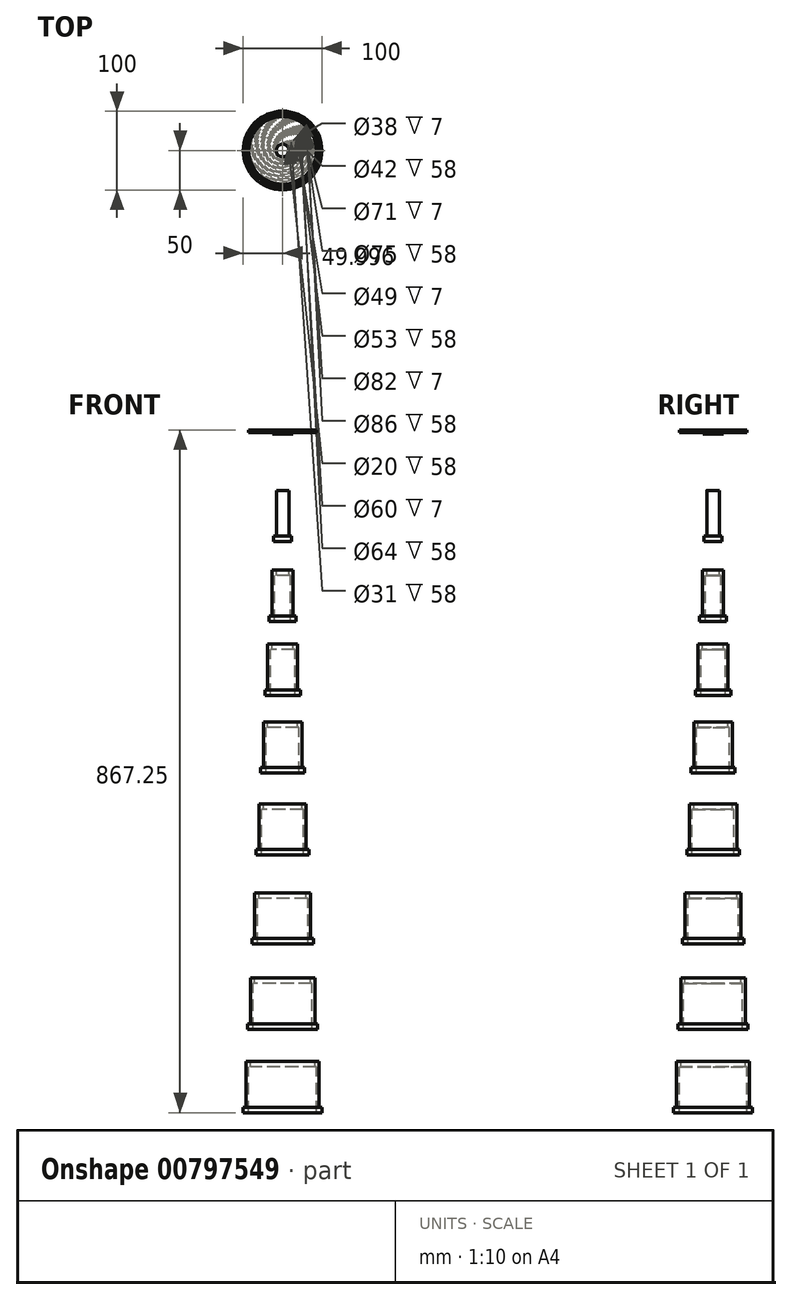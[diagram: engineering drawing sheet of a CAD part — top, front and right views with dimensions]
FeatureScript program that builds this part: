
annotation { "Feature Type Name" : "Feature", "Feature Type Description" : "" }
export const myFeature = defineFeature(function(context is Context, id is Id, definition is map)
    precondition{}
    {
        {
            var Q0;
            Q0=qCreatedBy(makeId("Front.planeOp"),FACE);
            var sketch = newSketch(context, id + "F0", { "sketchPlane" : qUnion([Q0])});
            skLineSegment(sketch, "E0", {"start": v(420.63, 136.3) * mm, "end": v(420.63, -631.8) * mm});
            skLineSegment(sketch, "E1", {"start": v(420.63, 28.97) * mm, "end": v(412.63, 28.97) * mm});
            skLineSegment(sketch, "E2", {"start": v(412.63, -34.03) * mm, "end": v(411.13, -34.03) * mm});
            skLineSegment(sketch, "E3", {"start": v(411.13, -34.03) * mm, "end": v(411.13, -41.03) * mm});
            skLineSegment(sketch, "E4", {"start": v(411.13, -41.03) * mm, "end": v(420.63, -41.03) * mm});
            skLineSegment(sketch, "E5", {"start": v(411.13, -54.93) * mm, "end": v(411.13, -61.93) * mm});
            skLineSegment(sketch, "E6", {"start": v(411.13, -61.93) * mm, "end": v(409.63, -61.93) * mm});
            skLineSegment(sketch, "E7", {"start": v(407.63, -112.93) * mm, "end": v(406.13, -112.93) * mm});
            skLineSegment(sketch, "E8", {"start": v(406.13, -112.93) * mm, "end": v(406.13, -119.93) * mm});
            skLineSegment(sketch, "E9", {"start": v(412.63, 52.64) * mm, "end": v(412.63, 57.64) * mm});
            skLineSegment(sketch, "E10", {"start": v(412.63, 57.64) * mm, "end": v(377.63, 57.64) * mm});
            skLineSegment(sketch, "E11", {"start": v(377.63, 57.64) * mm, "end": v(377.63, 54.64) * mm});
            skLineSegment(sketch, "E12", {"start": v(412.63, 52.64) * mm, "end": v(407.63, 52.64) * mm});
            skLineSegment(sketch, "E13", {"start": v(377.63, 54.64) * mm, "end": v(407.63, 54.64) * mm});
            skLineSegment(sketch, "E14", {"start": v(412.63, -34.03) * mm, "end": v(412.63, 28.97) * mm});
            skLineSegment(sketch, "E15", {"start": v(407.63, -112.93) * mm, "end": v(407.63, -54.93) * mm});
            skLineSegment(sketch, "E16", {"start": v(409.63, -119.93) * mm, "end": v(409.63, -61.93) * mm});
            skLineSegment(sketch, "E17", {"start": v(411.13, -34.03) * mm, "end": v(409.63, -34.03) * mm});
            skLineSegment(sketch, "E18", {"start": v(409.63, -34.03) * mm, "end": v(409.63, -41.03) * mm});
            skLineSegment(sketch, "E19", {"start": v(409.63, -41.03) * mm, "end": v(411.13, -41.03) * mm});
            skLineSegment(sketch, "E20", {"start": v(412.63, -61.93) * mm, "end": v(411.13, -61.93) * mm});
            skLineSegment(sketch, "E21", {"start": v(412.63, -61.93) * mm, "end": v(412.63, -54.93) * mm});
            skLineSegment(sketch, "E22", {"start": v(412.63, -54.93) * mm, "end": v(411.13, -54.93) * mm});
            skLineSegment(sketch, "E23", {"start": v(406.13, -119.93) * mm, "end": v(404.63, -119.93) * mm});
            skLineSegment(sketch, "E24", {"start": v(404.63, -119.93) * mm, "end": v(404.63, -112.93) * mm});
            skLineSegment(sketch, "E25", {"start": v(404.63, -112.93) * mm, "end": v(406.13, -112.93) * mm});
            skLineSegment(sketch, "E26", {"start": v(409.63, -61.93) * mm, "end": v(409.63, -54.93) * mm});
            skLineSegment(sketch, "E27", {"start": v(407.63, -112.93) * mm, "end": v(407.63, -119.93) * mm});
            skLineSegment(sketch, "E28", {"start": v(406.13, -119.93) * mm, "end": v(407.63, -119.93) * mm});
            skLineSegment(sketch, "E29", {"start": v(407.63, -119.93) * mm, "end": v(409.63, -119.93) * mm});
            skLineSegment(sketch, "E30", {"start": v(411.13, -54.93) * mm, "end": v(409.63, -54.93) * mm});
            skLineSegment(sketch, "E31", {"start": v(409.63, -54.93) * mm, "end": v(407.63, -54.93) * mm});
            skLineSegment(sketch, "E32", {"start": v(381.13, -577.9) * mm, "end": v(381.13, -584.9) * mm});
            skLineSegment(sketch, "E33", {"start": v(381.13, -584.9) * mm, "end": v(379.63, -584.9) * mm});
            skLineSegment(sketch, "E34", {"start": v(377.63, -632.9) * mm, "end": v(377.63, -577.9) * mm});
            skLineSegment(sketch, "E35", {"start": v(379.63, -642.9) * mm, "end": v(379.63, -584.9) * mm});
            skLineSegment(sketch, "E36", {"start": v(382.63, -584.9) * mm, "end": v(381.13, -584.9) * mm});
            skLineSegment(sketch, "E37", {"start": v(382.63, -584.9) * mm, "end": v(382.63, -577.9) * mm});
            skLineSegment(sketch, "E38", {"start": v(382.63, -577.9) * mm, "end": v(381.13, -577.9) * mm});
            skLineSegment(sketch, "E39", {"start": v(379.63, -584.9) * mm, "end": v(379.63, -577.9) * mm});
            skLineSegment(sketch, "E40", {"start": v(381.13, -577.9) * mm, "end": v(379.63, -577.9) * mm});
            skLineSegment(sketch, "E41", {"start": v(379.63, -577.9) * mm, "end": v(377.63, -577.9) * mm});
            skLineSegment(sketch, "E42.bottom", {"start": v(378.63, -642.9) * mm, "end": v(420.63, -642.9) * mm});
            skLineSegment(sketch, "E42.top", {"start": v(378.63, -649.9) * mm, "end": v(420.63, -649.9) * mm});
            skLineSegment(sketch, "E42.left", {"start": v(378.63, -642.9) * mm, "end": v(378.63, -649.9) * mm});
            skLineSegment(sketch, "E42.right", {"start": v(420.63, -642.9) * mm, "end": v(420.63, -649.9) * mm});
            skLineSegment(sketch, "E43", {"start": v(379.63, -642.9) * mm, "end": v(378.63, -642.9) * mm});
            skLineSegment(sketch, "E44", {"start": v(378.63, -649.9) * mm, "end": v(374.63, -649.9) * mm});
            skLineSegment(sketch, "E45", {"start": v(374.63, -649.9) * mm, "end": v(374.63, -632.9) * mm});
            skLineSegment(sketch, "E46", {"start": v(374.63, -632.9) * mm, "end": v(377.63, -632.9) * mm});
            skLineSegment(sketch, "E47", {"start": v(407.63, 54.64) * mm, "end": v(407.63, 52.64) * mm});
            skLineSegment(sketch, "E48.top", {"start": v(412.63, -64.93) * mm, "end": v(411.13, -64.93) * mm});
            skLineSegment(sketch, "E48.left", {"start": v(412.63, -61.93) * mm, "end": v(412.63, -64.93) * mm});
            skLineSegment(sketch, "E48.right", {"start": v(411.13, -61.93) * mm, "end": v(411.13, -64.93) * mm});
            skLineSegment(sketch, "E49", {"start": v(406.13, -136.28) * mm, "end": v(406.13, -143.28) * mm});
            skLineSegment(sketch, "E50", {"start": v(406.13, -143.28) * mm, "end": v(404.63, -143.28) * mm});
            skLineSegment(sketch, "E51", {"start": v(402.63, -194.28) * mm, "end": v(401.13, -194.28) * mm});
            skLineSegment(sketch, "E52", {"start": v(401.13, -194.28) * mm, "end": v(401.13, -201.28) * mm});
            skLineSegment(sketch, "E53", {"start": v(402.63, -194.28) * mm, "end": v(402.63, -136.28) * mm});
            skLineSegment(sketch, "E54", {"start": v(404.63, -201.28) * mm, "end": v(404.63, -143.28) * mm});
            skLineSegment(sketch, "E55", {"start": v(407.63, -143.28) * mm, "end": v(406.13, -143.28) * mm});
            skLineSegment(sketch, "E56", {"start": v(407.63, -143.28) * mm, "end": v(407.63, -136.28) * mm});
            skLineSegment(sketch, "E57", {"start": v(407.63, -136.28) * mm, "end": v(406.13, -136.28) * mm});
            skLineSegment(sketch, "E58", {"start": v(401.13, -201.28) * mm, "end": v(399.63, -201.28) * mm});
            skLineSegment(sketch, "E59", {"start": v(399.63, -201.28) * mm, "end": v(399.63, -194.28) * mm});
            skLineSegment(sketch, "E60", {"start": v(399.63, -194.28) * mm, "end": v(401.13, -194.28) * mm});
            skLineSegment(sketch, "E61", {"start": v(404.63, -143.28) * mm, "end": v(404.63, -136.28) * mm});
            skLineSegment(sketch, "E62", {"start": v(402.63, -194.28) * mm, "end": v(402.63, -201.28) * mm});
            skLineSegment(sketch, "E63", {"start": v(401.13, -201.28) * mm, "end": v(402.63, -201.28) * mm});
            skLineSegment(sketch, "E64", {"start": v(402.63, -201.28) * mm, "end": v(404.63, -201.28) * mm});
            skLineSegment(sketch, "E65", {"start": v(406.13, -136.28) * mm, "end": v(404.63, -136.28) * mm});
            skLineSegment(sketch, "E66", {"start": v(404.63, -136.28) * mm, "end": v(402.63, -136.28) * mm});
            skLineSegment(sketch, "E67.top", {"start": v(407.63, -146.28) * mm, "end": v(406.13, -146.28) * mm});
            skLineSegment(sketch, "E67.left", {"start": v(407.63, -143.28) * mm, "end": v(407.63, -146.28) * mm});
            skLineSegment(sketch, "E67.right", {"start": v(406.13, -143.28) * mm, "end": v(406.13, -146.28) * mm});
            skLineSegment(sketch, "E68", {"start": v(401.13, -219.28) * mm, "end": v(401.13, -226.28) * mm});
            skLineSegment(sketch, "E69", {"start": v(401.13, -226.28) * mm, "end": v(399.63, -226.28) * mm});
            skLineSegment(sketch, "E70", {"start": v(397.63, -277.28) * mm, "end": v(396.13, -277.28) * mm});
            skLineSegment(sketch, "E71", {"start": v(396.13, -277.28) * mm, "end": v(396.13, -284.28) * mm});
            skLineSegment(sketch, "E72", {"start": v(397.63, -277.28) * mm, "end": v(397.63, -219.28) * mm});
            skLineSegment(sketch, "E73", {"start": v(399.63, -284.28) * mm, "end": v(399.63, -226.28) * mm});
            skLineSegment(sketch, "E74", {"start": v(402.63, -226.28) * mm, "end": v(401.13, -226.28) * mm});
            skLineSegment(sketch, "E75", {"start": v(402.63, -226.28) * mm, "end": v(402.63, -219.28) * mm});
            skLineSegment(sketch, "E76", {"start": v(402.63, -219.28) * mm, "end": v(401.13, -219.28) * mm});
            skLineSegment(sketch, "E77", {"start": v(396.13, -284.28) * mm, "end": v(394.63, -284.28) * mm});
            skLineSegment(sketch, "E78", {"start": v(394.63, -284.28) * mm, "end": v(394.63, -277.28) * mm});
            skLineSegment(sketch, "E79", {"start": v(394.63, -277.28) * mm, "end": v(396.13, -277.28) * mm});
            skLineSegment(sketch, "E80", {"start": v(399.63, -226.28) * mm, "end": v(399.63, -219.28) * mm});
            skLineSegment(sketch, "E81", {"start": v(397.63, -277.28) * mm, "end": v(397.63, -284.28) * mm});
            skLineSegment(sketch, "E82", {"start": v(396.13, -284.28) * mm, "end": v(397.63, -284.28) * mm});
            skLineSegment(sketch, "E83", {"start": v(397.63, -284.28) * mm, "end": v(399.63, -284.28) * mm});
            skLineSegment(sketch, "E84", {"start": v(401.13, -219.28) * mm, "end": v(399.63, -219.28) * mm});
            skLineSegment(sketch, "E85", {"start": v(399.63, -219.28) * mm, "end": v(397.63, -219.28) * mm});
            skLineSegment(sketch, "E86.top", {"start": v(402.63, -229.28) * mm, "end": v(401.13, -229.28) * mm});
            skLineSegment(sketch, "E86.left", {"start": v(402.63, -226.28) * mm, "end": v(402.63, -229.28) * mm});
            skLineSegment(sketch, "E86.right", {"start": v(401.13, -226.28) * mm, "end": v(401.13, -229.28) * mm});
            skLineSegment(sketch, "E87", {"start": v(396.13, -311.87) * mm, "end": v(396.13, -318.87) * mm});
            skLineSegment(sketch, "E88", {"start": v(396.13, -318.87) * mm, "end": v(394.63, -318.87) * mm});
            skLineSegment(sketch, "E89", {"start": v(392.63, -369.87) * mm, "end": v(391.13, -369.87) * mm});
            skLineSegment(sketch, "E90", {"start": v(391.13, -369.87) * mm, "end": v(391.13, -376.87) * mm});
            skLineSegment(sketch, "E91", {"start": v(392.63, -369.87) * mm, "end": v(392.63, -311.87) * mm});
            skLineSegment(sketch, "E92", {"start": v(394.63, -376.87) * mm, "end": v(394.63, -318.87) * mm});
            skLineSegment(sketch, "E93", {"start": v(397.63, -318.87) * mm, "end": v(396.13, -318.87) * mm});
            skLineSegment(sketch, "E94", {"start": v(397.63, -318.87) * mm, "end": v(397.63, -311.87) * mm});
            skLineSegment(sketch, "E95", {"start": v(397.63, -311.87) * mm, "end": v(396.13, -311.87) * mm});
            skLineSegment(sketch, "E96", {"start": v(391.13, -376.87) * mm, "end": v(389.63, -376.87) * mm});
            skLineSegment(sketch, "E97", {"start": v(389.63, -376.87) * mm, "end": v(389.63, -369.87) * mm});
            skLineSegment(sketch, "E98", {"start": v(389.63, -369.87) * mm, "end": v(391.13, -369.87) * mm});
            skLineSegment(sketch, "E99", {"start": v(394.63, -318.87) * mm, "end": v(394.63, -311.87) * mm});
            skLineSegment(sketch, "E100", {"start": v(392.63, -369.87) * mm, "end": v(392.63, -376.87) * mm});
            skLineSegment(sketch, "E101", {"start": v(391.13, -376.87) * mm, "end": v(392.63, -376.87) * mm});
            skLineSegment(sketch, "E102", {"start": v(392.63, -376.87) * mm, "end": v(394.63, -376.87) * mm});
            skLineSegment(sketch, "E103", {"start": v(396.13, -311.87) * mm, "end": v(394.63, -311.87) * mm});
            skLineSegment(sketch, "E104", {"start": v(394.63, -311.87) * mm, "end": v(392.63, -311.87) * mm});
            skLineSegment(sketch, "E105.top", {"start": v(397.63, -321.87) * mm, "end": v(396.13, -321.87) * mm});
            skLineSegment(sketch, "E105.left", {"start": v(397.63, -318.87) * mm, "end": v(397.63, -321.87) * mm});
            skLineSegment(sketch, "E105.right", {"start": v(396.13, -318.87) * mm, "end": v(396.13, -321.87) * mm});
            skLineSegment(sketch, "E106", {"start": v(391.13, -394.77) * mm, "end": v(391.13, -401.77) * mm});
            skLineSegment(sketch, "E107", {"start": v(391.13, -401.77) * mm, "end": v(389.63, -401.77) * mm});
            skLineSegment(sketch, "E108", {"start": v(387.63, -452.77) * mm, "end": v(386.13, -452.77) * mm});
            skLineSegment(sketch, "E109", {"start": v(386.13, -452.77) * mm, "end": v(386.13, -459.77) * mm});
            skLineSegment(sketch, "E110", {"start": v(387.63, -452.77) * mm, "end": v(387.63, -394.77) * mm});
            skLineSegment(sketch, "E111", {"start": v(389.63, -459.77) * mm, "end": v(389.63, -401.77) * mm});
            skLineSegment(sketch, "E112", {"start": v(392.63, -401.77) * mm, "end": v(391.13, -401.77) * mm});
            skLineSegment(sketch, "E113", {"start": v(392.63, -401.77) * mm, "end": v(392.63, -394.77) * mm});
            skLineSegment(sketch, "E114", {"start": v(392.63, -394.77) * mm, "end": v(391.13, -394.77) * mm});
            skLineSegment(sketch, "E115", {"start": v(386.13, -459.77) * mm, "end": v(384.63, -459.77) * mm});
            skLineSegment(sketch, "E116", {"start": v(384.63, -459.77) * mm, "end": v(384.63, -452.77) * mm});
            skLineSegment(sketch, "E117", {"start": v(384.63, -452.77) * mm, "end": v(386.13, -452.77) * mm});
            skLineSegment(sketch, "E118", {"start": v(389.63, -401.77) * mm, "end": v(389.63, -394.77) * mm});
            skLineSegment(sketch, "E119", {"start": v(387.63, -452.77) * mm, "end": v(387.63, -459.77) * mm});
            skLineSegment(sketch, "E120", {"start": v(386.13, -459.77) * mm, "end": v(387.63, -459.77) * mm});
            skLineSegment(sketch, "E121", {"start": v(387.63, -459.77) * mm, "end": v(389.63, -459.77) * mm});
            skLineSegment(sketch, "E122", {"start": v(391.13, -394.77) * mm, "end": v(389.63, -394.77) * mm});
            skLineSegment(sketch, "E123", {"start": v(389.63, -394.77) * mm, "end": v(387.63, -394.77) * mm});
            skLineSegment(sketch, "E124.top", {"start": v(392.63, -404.77) * mm, "end": v(391.13, -404.77) * mm});
            skLineSegment(sketch, "E124.left", {"start": v(392.63, -401.77) * mm, "end": v(392.63, -404.77) * mm});
            skLineSegment(sketch, "E124.right", {"start": v(391.13, -401.77) * mm, "end": v(391.13, -404.77) * mm});
            skLineSegment(sketch, "E125", {"start": v(386.13, -485.67) * mm, "end": v(386.13, -492.67) * mm});
            skLineSegment(sketch, "E126", {"start": v(386.13, -492.67) * mm, "end": v(384.63, -492.67) * mm});
            skLineSegment(sketch, "E127", {"start": v(382.63, -543.67) * mm, "end": v(381.13, -543.67) * mm});
            skLineSegment(sketch, "E128", {"start": v(381.13, -543.67) * mm, "end": v(381.13, -550.67) * mm});
            skLineSegment(sketch, "E129", {"start": v(382.63, -543.67) * mm, "end": v(382.63, -485.67) * mm});
            skLineSegment(sketch, "E130", {"start": v(384.63, -550.67) * mm, "end": v(384.63, -492.67) * mm});
            skLineSegment(sketch, "E131", {"start": v(387.63, -492.67) * mm, "end": v(386.13, -492.67) * mm});
            skLineSegment(sketch, "E132", {"start": v(387.63, -492.67) * mm, "end": v(387.63, -485.67) * mm});
            skLineSegment(sketch, "E133", {"start": v(387.63, -485.67) * mm, "end": v(386.13, -485.67) * mm});
            skLineSegment(sketch, "E134", {"start": v(381.13, -550.67) * mm, "end": v(379.63, -550.67) * mm});
            skLineSegment(sketch, "E135", {"start": v(379.63, -550.67) * mm, "end": v(379.63, -543.67) * mm});
            skLineSegment(sketch, "E136", {"start": v(379.63, -543.67) * mm, "end": v(381.13, -543.67) * mm});
            skLineSegment(sketch, "E137", {"start": v(384.63, -492.67) * mm, "end": v(384.63, -485.67) * mm});
            skLineSegment(sketch, "E138", {"start": v(382.63, -543.67) * mm, "end": v(382.63, -550.67) * mm});
            skLineSegment(sketch, "E139", {"start": v(381.13, -550.67) * mm, "end": v(382.63, -550.67) * mm});
            skLineSegment(sketch, "E140", {"start": v(382.63, -550.67) * mm, "end": v(384.63, -550.67) * mm});
            skLineSegment(sketch, "E141", {"start": v(386.13, -485.67) * mm, "end": v(384.63, -485.67) * mm});
            skLineSegment(sketch, "E142", {"start": v(384.63, -485.67) * mm, "end": v(382.63, -485.67) * mm});
            skLineSegment(sketch, "E143.top", {"start": v(387.63, -495.67) * mm, "end": v(386.13, -495.67) * mm});
            skLineSegment(sketch, "E143.left", {"start": v(387.63, -492.67) * mm, "end": v(387.63, -495.67) * mm});
            skLineSegment(sketch, "E143.right", {"start": v(386.13, -492.67) * mm, "end": v(386.13, -495.67) * mm});
            skLineSegment(sketch, "E144.left", {"start": v(420.63, 28.97) * mm, "end": v(420.63, 18.97) * mm});
            skLineSegment(sketch, "E145", {"start": v(762.6, 130.32) * mm, "end": v(762.6, -637.77) * mm, "construction": true});
            skLineSegment(sketch, "E146", {"start": v(762.6, -10.86) * mm, "end": v(754.6, -10.86) * mm});
            skLineSegment(sketch, "E147", {"start": v(754.6, -10.86) * mm, "end": v(754.6, -68.86) * mm});
            skLineSegment(sketch, "E148", {"start": v(754.6, -68.86) * mm, "end": v(752.6, -68.86) * mm});
            skLineSegment(sketch, "E149", {"start": v(752.6, -68.86) * mm, "end": v(751.1, -68.86) * mm});
            skLineSegment(sketch, "E150", {"start": v(751.1, -68.86) * mm, "end": v(751.1, -75.86) * mm});
            skLineSegment(sketch, "E151", {"start": v(751.1, -75.86) * mm, "end": v(762.6, -75.86) * mm});
            skLineSegment(sketch, "E152", {"start": v(762.6, -75.86) * mm, "end": v(762.6, -10.86) * mm});
            skLineSegment(sketch, "E153", {"start": v(754.6, -112.1) * mm, "end": v(752.6, -112.1) * mm});
            skLineSegment(sketch, "E154", {"start": v(752.6, -112.1) * mm, "end": v(751.1, -112.1) * mm});
            skLineSegment(sketch, "E155", {"start": v(751.1, -112.1) * mm, "end": v(749.1, -112.1) * mm});
            skLineSegment(sketch, "E156", {"start": v(749.1, -112.1) * mm, "end": v(749.1, -170.1) * mm});
            skLineSegment(sketch, "E157", {"start": v(749.1, -170.1) * mm, "end": v(747.1, -170.1) * mm});
            skLineSegment(sketch, "E158", {"start": v(747.1, -170.1) * mm, "end": v(745.6, -170.1) * mm});
            skLineSegment(sketch, "E159", {"start": v(745.6, -170.1) * mm, "end": v(745.6, -177.1) * mm});
            skLineSegment(sketch, "E160", {"start": v(754.6, -112.1) * mm, "end": v(754.6, -119.1) * mm});
            skLineSegment(sketch, "E161", {"start": v(754.6, -119.1) * mm, "end": v(752.6, -119.1) * mm});
            skLineSegment(sketch, "E162", {"start": v(752.6, -119.1) * mm, "end": v(752.6, -177.1) * mm});
            skLineSegment(sketch, "E163", {"start": v(752.6, -177.1) * mm, "end": v(745.6, -177.1) * mm});
            skLineSegment(sketch, "E164", {"start": v(749.1, -206.1) * mm, "end": v(747.1, -206.1) * mm});
            skLineSegment(sketch, "E165", {"start": v(747.1, -206.1) * mm, "end": v(745.6, -206.1) * mm});
            skLineSegment(sketch, "E166", {"start": v(745.6, -206.1) * mm, "end": v(743.6, -206.1) * mm});
            skLineSegment(sketch, "E167", {"start": v(743.6, -206.1) * mm, "end": v(743.6, -264.1) * mm});
            skLineSegment(sketch, "E168", {"start": v(743.6, -264.1) * mm, "end": v(741.6, -264.1) * mm});
            skLineSegment(sketch, "E169", {"start": v(741.6, -264.1) * mm, "end": v(740.1, -264.1) * mm});
            skLineSegment(sketch, "E170", {"start": v(740.1, -264.1) * mm, "end": v(740.1, -271.1) * mm});
            skLineSegment(sketch, "E171", {"start": v(749.1, -206.1) * mm, "end": v(749.1, -213.1) * mm});
            skLineSegment(sketch, "E172", {"start": v(749.1, -213.1) * mm, "end": v(747.1, -213.1) * mm});
            skLineSegment(sketch, "E173", {"start": v(747.1, -213.1) * mm, "end": v(747.1, -271.1) * mm});
            skLineSegment(sketch, "E174", {"start": v(747.1, -271.1) * mm, "end": v(740.1, -271.1) * mm});
            skLineSegment(sketch, "E175", {"start": v(743.6, -304.87) * mm, "end": v(741.6, -304.87) * mm});
            skLineSegment(sketch, "E176", {"start": v(741.6, -304.87) * mm, "end": v(740.1, -304.87) * mm});
            skLineSegment(sketch, "E177", {"start": v(740.1, -304.87) * mm, "end": v(738.1, -304.87) * mm});
            skLineSegment(sketch, "E178", {"start": v(738.1, -304.87) * mm, "end": v(738.1, -362.87) * mm});
            skLineSegment(sketch, "E179", {"start": v(738.1, -362.87) * mm, "end": v(736.1, -362.87) * mm});
            skLineSegment(sketch, "E180", {"start": v(736.1, -362.87) * mm, "end": v(734.6, -362.87) * mm});
            skLineSegment(sketch, "E181", {"start": v(734.6, -362.87) * mm, "end": v(734.6, -369.87) * mm});
            skLineSegment(sketch, "E182", {"start": v(743.6, -304.87) * mm, "end": v(743.6, -311.87) * mm});
            skLineSegment(sketch, "E183", {"start": v(743.6, -311.87) * mm, "end": v(741.6, -311.87) * mm});
            skLineSegment(sketch, "E184", {"start": v(741.6, -311.87) * mm, "end": v(741.6, -369.87) * mm});
            skLineSegment(sketch, "E185", {"start": v(741.6, -369.87) * mm, "end": v(734.6, -369.87) * mm});
            skLineSegment(sketch, "E186", {"start": v(738.1, -408.87) * mm, "end": v(736.1, -408.87) * mm});
            skLineSegment(sketch, "E187", {"start": v(736.1, -408.87) * mm, "end": v(734.6, -408.87) * mm});
            skLineSegment(sketch, "E188", {"start": v(734.6, -408.87) * mm, "end": v(732.6, -408.87) * mm});
            skLineSegment(sketch, "E189", {"start": v(732.6, -408.87) * mm, "end": v(732.6, -466.87) * mm});
            skLineSegment(sketch, "E190", {"start": v(732.6, -466.87) * mm, "end": v(730.6, -466.87) * mm});
            skLineSegment(sketch, "E191", {"start": v(730.6, -466.87) * mm, "end": v(729.1, -466.87) * mm});
            skLineSegment(sketch, "E192", {"start": v(729.1, -466.87) * mm, "end": v(729.1, -473.87) * mm});
            skLineSegment(sketch, "E193", {"start": v(738.1, -408.87) * mm, "end": v(738.1, -415.87) * mm});
            skLineSegment(sketch, "E194", {"start": v(738.1, -415.87) * mm, "end": v(736.1, -415.87) * mm});
            skLineSegment(sketch, "E195", {"start": v(736.1, -415.87) * mm, "end": v(736.1, -473.87) * mm});
            skLineSegment(sketch, "E196", {"start": v(736.1, -473.87) * mm, "end": v(729.1, -473.87) * mm});
            skLineSegment(sketch, "E197", {"start": v(732.6, -522.18) * mm, "end": v(730.6, -522.18) * mm});
            skLineSegment(sketch, "E198", {"start": v(730.6, -522.18) * mm, "end": v(729.1, -522.18) * mm});
            skLineSegment(sketch, "E199", {"start": v(729.1, -522.18) * mm, "end": v(727.1, -522.18) * mm});
            skLineSegment(sketch, "E200", {"start": v(727.1, -522.18) * mm, "end": v(727.1, -580.18) * mm});
            skLineSegment(sketch, "E201", {"start": v(727.1, -580.18) * mm, "end": v(725.1, -580.18) * mm});
            skLineSegment(sketch, "E202", {"start": v(725.1, -580.18) * mm, "end": v(723.6, -580.18) * mm});
            skLineSegment(sketch, "E203", {"start": v(723.6, -580.18) * mm, "end": v(723.6, -587.18) * mm});
            skLineSegment(sketch, "E204", {"start": v(732.6, -522.18) * mm, "end": v(732.6, -529.18) * mm});
            skLineSegment(sketch, "E205", {"start": v(732.6, -529.18) * mm, "end": v(730.6, -529.18) * mm});
            skLineSegment(sketch, "E206", {"start": v(730.6, -529.18) * mm, "end": v(730.6, -587.18) * mm});
            skLineSegment(sketch, "E207", {"start": v(730.6, -587.18) * mm, "end": v(723.6, -587.18) * mm});
            skLineSegment(sketch, "E208", {"start": v(727.1, -630.23) * mm, "end": v(725.1, -630.23) * mm});
            skLineSegment(sketch, "E209", {"start": v(725.1, -630.23) * mm, "end": v(723.6, -630.23) * mm});
            skLineSegment(sketch, "E210", {"start": v(723.6, -630.23) * mm, "end": v(721.6, -630.23) * mm});
            skLineSegment(sketch, "E211", {"start": v(721.6, -630.23) * mm, "end": v(721.6, -688.23) * mm});
            skLineSegment(sketch, "E212", {"start": v(721.6, -688.23) * mm, "end": v(719.6, -688.23) * mm});
            skLineSegment(sketch, "E213", {"start": v(719.6, -688.23) * mm, "end": v(718.1, -688.23) * mm});
            skLineSegment(sketch, "E214", {"start": v(718.1, -688.23) * mm, "end": v(718.1, -695.23) * mm});
            skLineSegment(sketch, "E215", {"start": v(727.1, -630.23) * mm, "end": v(727.1, -637.23) * mm});
            skLineSegment(sketch, "E216", {"start": v(727.1, -637.23) * mm, "end": v(725.1, -637.23) * mm});
            skLineSegment(sketch, "E217", {"start": v(725.1, -637.23) * mm, "end": v(725.1, -695.23) * mm});
            skLineSegment(sketch, "E218", {"start": v(725.1, -695.23) * mm, "end": v(718.1, -695.23) * mm});
            skLineSegment(sketch, "E219", {"start": v(721.6, -736.28) * mm, "end": v(719.6, -736.28) * mm});
            skLineSegment(sketch, "E220", {"start": v(719.6, -736.28) * mm, "end": v(718.1, -736.28) * mm});
            skLineSegment(sketch, "E221", {"start": v(718.1, -736.28) * mm, "end": v(716.1, -736.28) * mm});
            skLineSegment(sketch, "E222", {"start": v(716.1, -736.28) * mm, "end": v(716.1, -794.28) * mm});
            skLineSegment(sketch, "E223", {"start": v(716.1, -794.28) * mm, "end": v(714.1, -794.28) * mm});
            skLineSegment(sketch, "E224", {"start": v(714.1, -794.28) * mm, "end": v(712.6, -794.28) * mm});
            skLineSegment(sketch, "E225", {"start": v(712.6, -794.28) * mm, "end": v(712.6, -801.28) * mm});
            skLineSegment(sketch, "E226", {"start": v(721.6, -736.28) * mm, "end": v(721.6, -743.28) * mm});
            skLineSegment(sketch, "E227", {"start": v(721.6, -743.28) * mm, "end": v(719.6, -743.28) * mm});
            skLineSegment(sketch, "E228", {"start": v(719.6, -743.28) * mm, "end": v(719.6, -801.28) * mm});
            skLineSegment(sketch, "E229", {"start": v(719.6, -801.28) * mm, "end": v(712.6, -801.28) * mm});
            skLineSegment(sketch, "E230", {"start": v(754.6, 60.97) * mm, "end": v(754.6, 65.97) * mm});
            skLineSegment(sketch, "E231", {"start": v(754.6, 65.97) * mm, "end": v(719.6, 65.97) * mm});
            skLineSegment(sketch, "E232", {"start": v(719.6, 65.97) * mm, "end": v(719.6, 62.97) * mm});
            skLineSegment(sketch, "E233", {"start": v(754.6, 60.97) * mm, "end": v(749.6, 60.97) * mm});
            skLineSegment(sketch, "E234", {"start": v(719.6, 62.97) * mm, "end": v(749.6, 62.97) * mm});
            skLineSegment(sketch, "E235", {"start": v(749.6, 62.97) * mm, "end": v(749.6, 60.97) * mm});
            skSolve(sketch);
        }
        {
            var Q0;
            Q0=makeQuery(id+"F0.imprint","IMPRINT",FACE,{"disambiguationData":[TD([[makeQuery(id+"F0.imprint","IMPRINT",EDGE,{"derivedFrom":sQuery(id+"F0.wireOp",EDGE,"E230")}),1.0]])]});
            var Q1;
            Q1=makeQuery(id+"F0.imprint","IMPRINT",FACE,{"disambiguationData":[TD([[makeQuery(id+"F0.imprint","IMPRINT",EDGE,{"derivedFrom":sQuery(id+"F0.wireOp",EDGE,"E146")}),1.0]])]});
            var Q2;
            Q2=makeQuery(id+"F0.imprint","IMPRINT",FACE,{"disambiguationData":[TD([[makeQuery(id+"F0.imprint","IMPRINT",EDGE,{"derivedFrom":sQuery(id+"F0.wireOp",EDGE,"E153")}),1.0]])]});
            var Q3;
            Q3=makeQuery(id+"F0.imprint","IMPRINT",FACE,{"disambiguationData":[TD([[makeQuery(id+"F0.imprint","IMPRINT",EDGE,{"derivedFrom":sQuery(id+"F0.wireOp",EDGE,"E164")}),1.0]])]});
            var Q4;
            Q4=makeQuery(id+"F0.imprint","IMPRINT",FACE,{"disambiguationData":[TD([[makeQuery(id+"F0.imprint","IMPRINT",EDGE,{"derivedFrom":sQuery(id+"F0.wireOp",EDGE,"E175")}),1.0]])]});
            var Q5;
            Q5=makeQuery(id+"F0.imprint","IMPRINT",FACE,{"disambiguationData":[TD([[makeQuery(id+"F0.imprint","IMPRINT",EDGE,{"derivedFrom":sQuery(id+"F0.wireOp",EDGE,"E186")}),1.0]])]});
            var Q6;
            Q6=makeQuery(id+"F0.imprint","IMPRINT",FACE,{"disambiguationData":[TD([[makeQuery(id+"F0.imprint","IMPRINT",EDGE,{"derivedFrom":sQuery(id+"F0.wireOp",EDGE,"E197")}),1.0]])]});
            var Q7;
            Q7=makeQuery(id+"F0.imprint","IMPRINT",FACE,{"disambiguationData":[TD([[makeQuery(id+"F0.imprint","IMPRINT",EDGE,{"derivedFrom":sQuery(id+"F0.wireOp",EDGE,"E208")}),1.0]])]});
            var Q8;
            Q8=makeQuery(id+"F0.imprint","IMPRINT",FACE,{"disambiguationData":[TD([[makeQuery(id+"F0.imprint","IMPRINT",EDGE,{"derivedFrom":sQuery(id+"F0.wireOp",EDGE,"E219")}),1.0]])]});
            var Q9;
            Q9=sQuery(id+"F0.wireOp",EDGE,"E145");
            revolve(context, id + "F1", {"surfaceOperationType" : NewSurfaceOperationType.NEW, "entities" : qUnion([Q0, Q1, Q2, Q3, Q4, Q5, Q6, Q7, Q8]), "axis" : qUnion([Q9]), "revolveType" : RevolveType.FULL});
        }
    });
